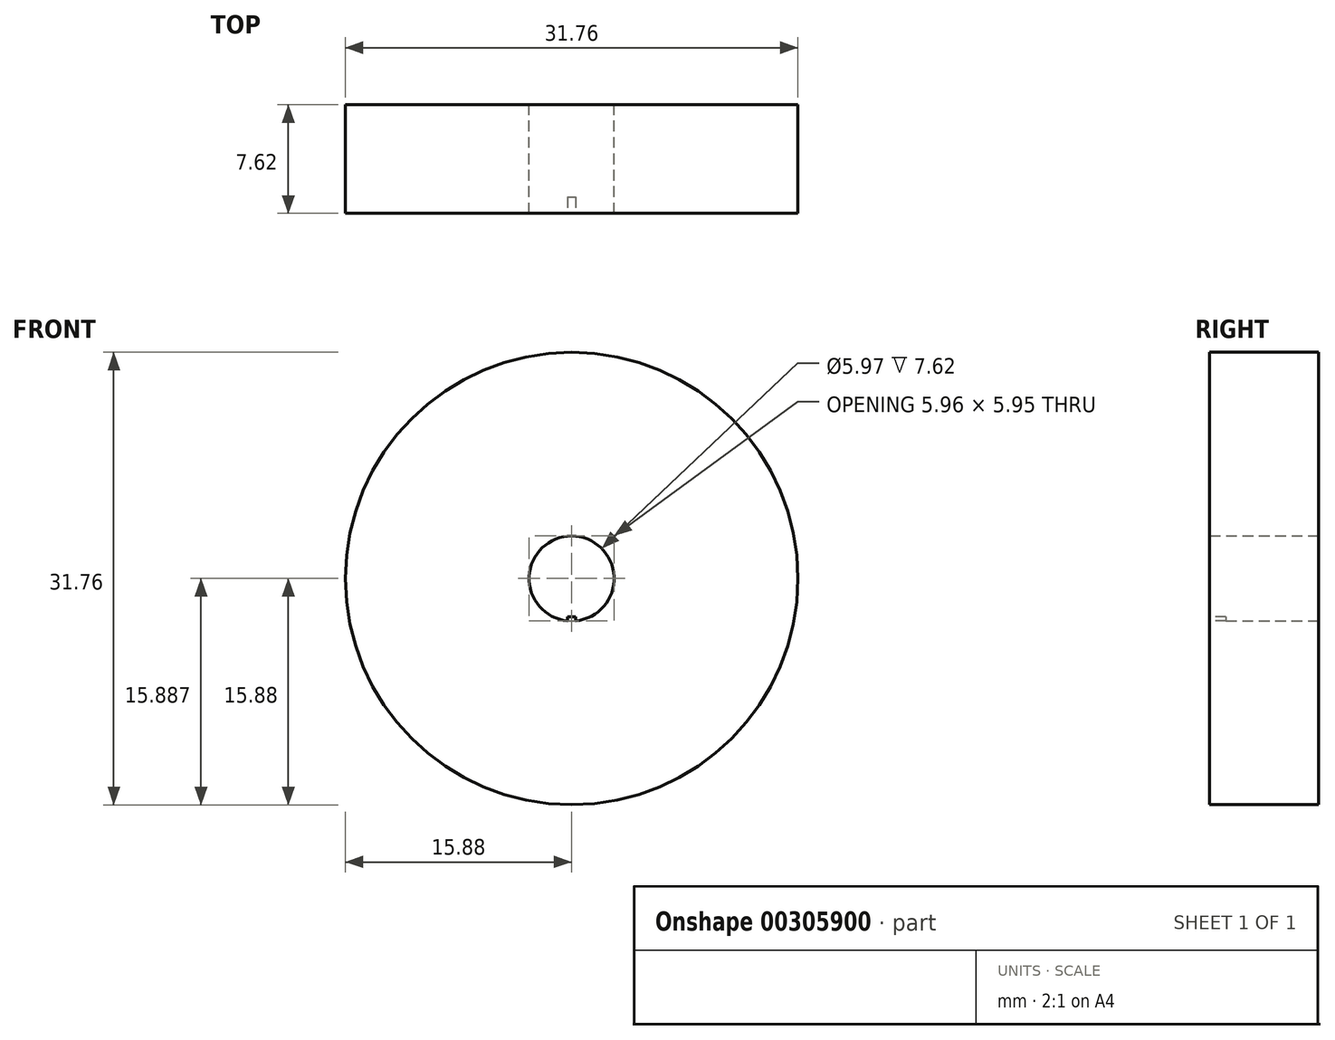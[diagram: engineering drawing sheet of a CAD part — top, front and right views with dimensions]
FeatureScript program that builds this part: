
annotation { "Feature Type Name" : "Feature", "Feature Type Description" : "" }
export const myFeature = defineFeature(function(context is Context, id is Id, definition is map)
    precondition{}
    {
        {
            var Q0;
            Q0=qCreatedBy(makeId("Front.planeOp"),FACE);
            var sketch = newSketch(context, id + "F0", { "sketchPlane" : qUnion([Q0])});
            skCircle(sketch, "E0", {"center": v(0, 0) * mm, "radius": 15.88 * mm});
            skCircle(sketch, "E1", {"center": v(0, 0) * mm, "radius": 2.98 * mm});
            skSolve(sketch);
        }
        {
            var Q0;
            Q0=makeQuery(id+"F0.imprint","IMPRINT",FACE,{"disambiguationData":[TD([[makeQuery(id+"F0.imprint","IMPRINT",EDGE,{"derivedFrom":sQuery(id+"F0.wireOp",EDGE,"E0")}),1.0]])]});
            extrude(context, id + "F1", {"entities" : qUnion([Q0]), "depth" : 7.62 * mm});
        }
        {
            var Q0;
            Q0=makeQuery(id+"F1.opExtrude","CAP_FACE",FACE,{"disambiguationData":[OSD([sQuery(id+"F0.wireOp",EDGE,"E0"),sQuery(id+"F0.wireOp",EDGE,"E1")])],"isStart":false});
            var sketch = newSketch(context, id + "F2", { "sketchPlane" : qUnion([Q0])});
            skLineSegment(sketch, "E2.bottom", {"start": v(-0.3, -2.7) * mm, "end": v(0.3, -2.7) * mm});
            skLineSegment(sketch, "E2.top", {"start": v(-0.3, -3.28) * mm, "end": v(0.3, -3.28) * mm});
            skLineSegment(sketch, "E2.left", {"start": v(-0.3, -2.7) * mm, "end": v(-0.3, -3.28) * mm});
            skLineSegment(sketch, "E2.right", {"start": v(0.3, -2.7) * mm, "end": v(0.3, -3.28) * mm});
            skPoint(sketch, "E2.middle", {"position": v(0, -2.98) * mm});
            skSolve(sketch);
        }
        {
            var Q0;
            {var subQ0=sQuery(id+"F2.wireOp",EDGE,"E2.bottom");Q0=makeQuery(id+"F2.imprint","IMPRINT",FACE,{"disambiguationData":[TD([[makeQuery(id+"F2.imprint","IMPRINT",EDGE,{"derivedFrom":subQ0}),-1.0]])]});}
            extrude(context, id + "F3", {"entities" : qUnion([Q0]), "operationType" : NewBodyOperationType.ADD, "oppositeDirection" : true, "depth" : 1.14 * mm});
        }
    });
